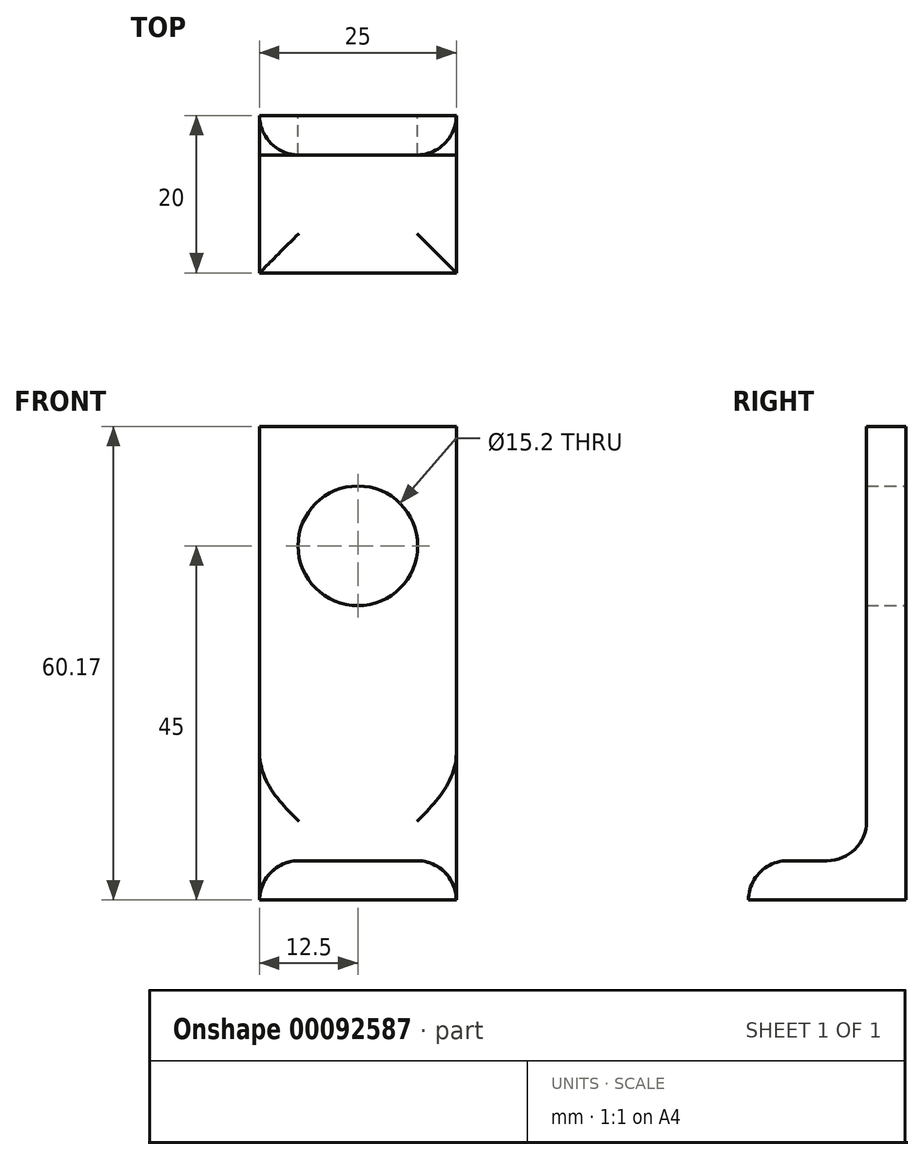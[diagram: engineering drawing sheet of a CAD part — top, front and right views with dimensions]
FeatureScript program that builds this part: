
annotation { "Feature Type Name" : "Feature", "Feature Type Description" : "" }
export const myFeature = defineFeature(function(context is Context, id is Id, definition is map)
    precondition{}
    {
        {
            var Q0;
            Q0=qCreatedBy(makeId("Front.planeOp"),FACE);
            var sketch = newSketch(context, id + "F0", { "sketchPlane" : qUnion([Q0])});
            skLineSegment(sketch, "E0.bottom", {"start": v(12.5, -22.5) * mm, "end": v(-12.5, -22.5) * mm});
            skLineSegment(sketch, "E0.top", {"start": v(12.5, 22.5) * mm, "end": v(-12.5, 22.5) * mm});
            skLineSegment(sketch, "E0.left", {"start": v(12.5, -22.5) * mm, "end": v(12.5, 22.5) * mm});
            skLineSegment(sketch, "E0.right", {"start": v(-12.5, -22.5) * mm, "end": v(-12.5, 22.5) * mm});
            skPoint(sketch, "E0.middle", {"position": v(0, 0) * mm});
            skCircle(sketch, "E1", {"center": v(0, 22.5) * mm, "radius": 7.6 * mm});
            skLineSegment(sketch, "E2.bottom", {"start": v(-12.5, 22.5) * mm, "end": v(12.5, 22.5) * mm});
            skLineSegment(sketch, "E2.top", {"start": v(-12.5, 37.67) * mm, "end": v(12.5, 37.67) * mm});
            skLineSegment(sketch, "E2.left", {"start": v(-12.5, 22.5) * mm, "end": v(-12.5, 37.67) * mm});
            skLineSegment(sketch, "E2.right", {"start": v(12.5, 22.5) * mm, "end": v(12.5, 37.67) * mm});
            skSolve(sketch);
        }
        {
            var Q0;
            Q0=makeQuery(id+"F0.imprint","IMPRINT",FACE,{"disambiguationData":[TD([[makeQuery(id+"F0.imprint","IMPRINT",EDGE,{"derivedFrom":sQuery(id+"F0.wireOp",EDGE,"E0.bottom")}),-1.0]])]});
            var Q1;
            Q1=makeQuery(id+"F0.imprint","IMPRINT",FACE,{"disambiguationData":[TD([[makeQuery(id+"F0.imprint","IMPRINT",EDGE,{"derivedFrom":sQuery(id+"F0.wireOp",EDGE,"E2.top")}),-1.0]])]});
            extrude(context, id + "F1", {"entities" : qUnion([Q0, Q1]), "depth" : 5 * mm});
        }
        {
            var Q0;
            Q0=makeQuery(id+"F1.opExtrude","CAP_FACE",FACE,{"disambiguationData":[OSD([sQuery(id+"F0.wireOp",EDGE,"E0.bottom"),sQuery(id+"F0.wireOp",EDGE,"E0.top"),sQuery(id+"F0.wireOp",EDGE,"E0.left"),sQuery(id+"F0.wireOp",EDGE,"E0.right"),sQuery(id+"F0.wireOp",EDGE,"E1")])],"isStart":false});
            var sketch = newSketch(context, id + "F2", { "sketchPlane" : qUnion([Q0])});
            skLineSegment(sketch, "E3.bottom", {"start": v(-12.5, -22.5) * mm, "end": v(12.5, -22.5) * mm});
            skLineSegment(sketch, "E3.top", {"start": v(-12.5, -17.5) * mm, "end": v(12.5, -17.5) * mm});
            skLineSegment(sketch, "E3.left", {"start": v(-12.5, -22.5) * mm, "end": v(-12.5, -17.5) * mm});
            skLineSegment(sketch, "E3.right", {"start": v(12.5, -22.5) * mm, "end": v(12.5, -17.5) * mm});
            skSolve(sketch);
        }
        {
            var Q0;
            Q0=makeQuery(id+"F2.imprint","IMPRINT",FACE,{"disambiguationData":[TD([[makeQuery(id+"F2.imprint","IMPRINT",EDGE,{"derivedFrom":sQuery(id+"F2.wireOp",EDGE,"E3.bottom")}),-1.0]])]});
            extrude(context, id + "F3", {"entities" : qUnion([Q0]), "operationType" : NewBodyOperationType.ADD, "depth" : 15 * mm});
        }
        {
            var Q0;
            Q0=makeQuery(id+"F3.opExtrude","SWEPT_FACE",FACE,{"disambiguationData":[OSD([sQuery(id+"F2.wireOp",EDGE,"E3.top")])]});
            fillet(context, id + "F4", {"entities" : qUnion([Q0]), "radius" : 5 * mm, "tangentPropagation" : true, "allowEdgeOverflow" : false});
        }
    });
